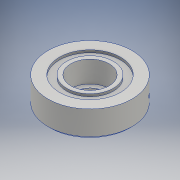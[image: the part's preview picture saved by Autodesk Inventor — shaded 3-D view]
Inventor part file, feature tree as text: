
AUTODESK INVENTOR PART (.ipt)
format: ipt  version: 2017 (Build 210142000, 142)  size: 200,192 bytes
history: native  units: mm
features: sketch x9, thread x8, hole x5, plane x4, extrude x3, chamfer x1, projected_geometry x1
ambient origin geometry x8: Origin, YZ Plane, XZ Plane, XY Plane, X Axis, Y Axis, Z Axis, Center Point
bodies: Solid1 (feature_tree)
feature tree (31):
  extrude  "Extrusion1"  Depth=24.0mm
  extrude  "Extrusion2"  Depth=51.0mm
  sketch  "Sketch3"  dims[d5=6.0mm d6=2.1mm d7=0.0mm]
  plane  "Work Plane1"
  plane  "Work Plane2"
  plane  "Work Plane3"
  plane  "Work Plane4"
  hole  "Hole1"  [1 undecoded]
  hole  "Hole2"  [1 undecoded]
  hole  "Hole3"  [1 undecoded]
  hole  "Hole4"  [1 undecoded]
  thread  "Thread1"  [1 undecoded]
  thread  "Thread2"  [1 undecoded]
  thread  "Thread3"  [1 undecoded]
  thread  "Thread4"  [1 undecoded]
  extrude  "Extrusion3"  Depth=10.0mm TaperAngle=0.0deg
  hole  "Hole6"  [1 undecoded]
  thread  "Thread9"  [1 undecoded]
  thread  "Thread10"  [1 undecoded]
  thread  "Thread11"  [1 undecoded]
  thread  "Thread12"  [1 undecoded]
  chamfer  "Chamfer2"  Distance=10.0mm
  sketch  "Sketch1"  dims[d0=70.0mm d1=24.0mm]
  sketch  "Sketch2"  dims[d2=22.0mm d3=0.0mm d4=51.0mm]
  projected_geometry  "Projected Loop1"
  sketch  "Sketch4"  dims[d11=6.981317mm d12=60.0deg]
  sketch  "Sketch5"  dims[d13=13.0mm]
  sketch  "Sketch6"  dims[d14=3.0mm d15=6.0mm d16=4.0mm d17=2.0mm d18=90.0deg d19=4.0mm d20=20.594885mm d21=13.0mm]
  sketch  "Sketch7"  dims[d22=3.0mm d23=6.0mm d24=4.0mm d25=2.0mm d26=90.0deg d27=8.0mm d28=20.594885mm d29=13.0mm]
  sketch  "Sketch9"  dims[d30=3.0mm d31=6.0mm d32=4.0mm d33=2.0mm d34=90.0deg d35=8.0mm d36=20.594885mm d37=13.0mm]
  sketch  "Sketch11"  dims[d38=3.0mm d39=6.0mm d40=4.0mm d41=2.0mm d42=90.0deg d43=8.0mm d44=20.594885mm d45=10.0mm d46=0.0mm d47=10.0mm d48=0.0mm d49=10.0mm d50=0.0mm d51=10.0mm d52=0.0mm d53=32.0mm d54=18.0mm d55=0.0mm d77=54.0mm d78=40.0mm d80=360.0deg d82=3.0mm d83=6.0mm d84=4.0mm d85=2.0mm d86=90.0deg d87=8.0mm d88=20.594885mm d89=10.0mm d90=0.0mm d91=10.0mm d92=0.0mm d93=10.0mm d94=0.0mm d95=10.0mm d96=0.0mm d97=2.0mm d98=2.0mm d99=45.0deg]
note: 13 required parameter values undecoded (feature->parameter linkage not recoverable at this tier; creation-order binding heuristic only, values carry confidence <= 0.55)
